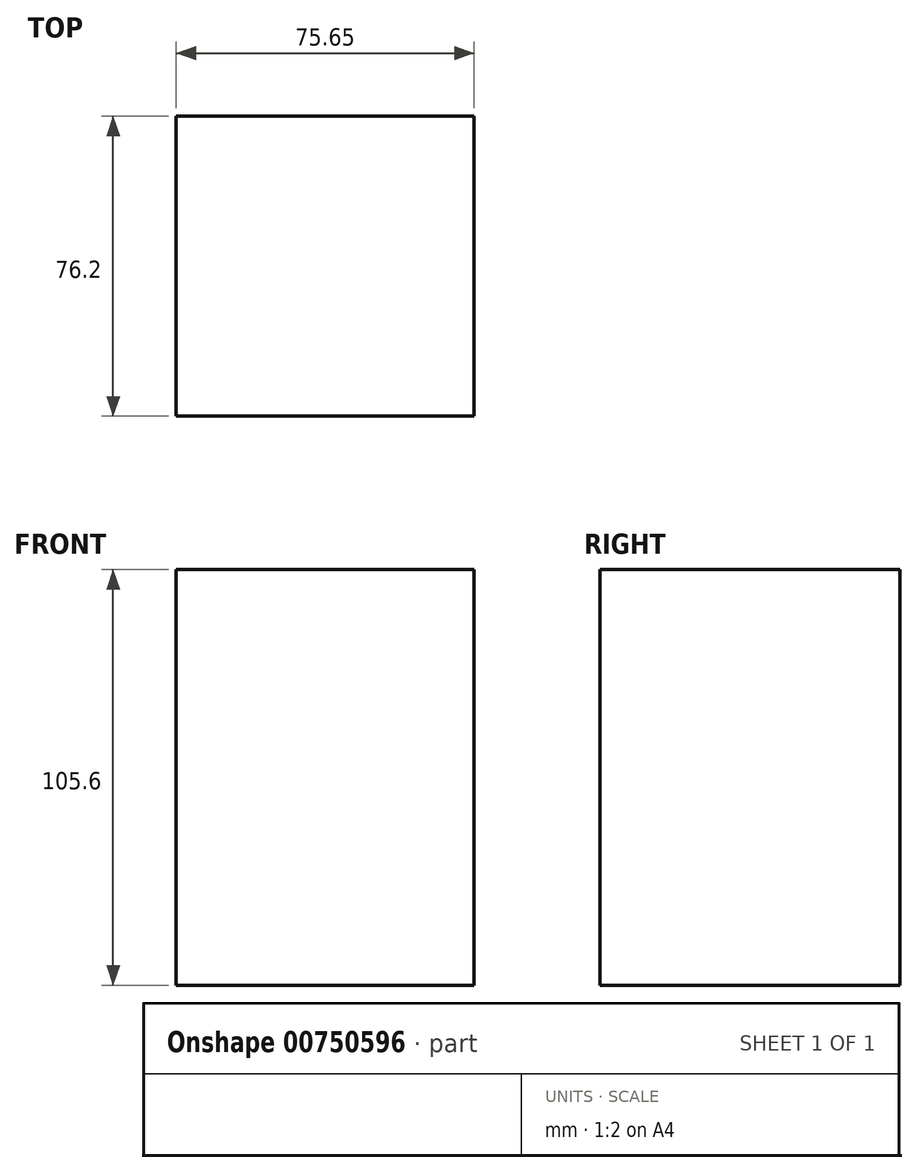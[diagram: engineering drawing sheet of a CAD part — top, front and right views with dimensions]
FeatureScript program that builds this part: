
annotation { "Feature Type Name" : "Feature", "Feature Type Description" : "" }
export const myFeature = defineFeature(function(context is Context, id is Id, definition is map)
    precondition{}
    {
        {
            var Q0;
            Q0=qCreatedBy(makeId("Front.planeOp"),FACE);
            var sketch = newSketch(context, id + "F0", { "sketchPlane" : qUnion([Q0])});
            skLineSegment(sketch, "E0.bottom", {"start": v(-38.96, 42.94) * mm, "end": v(36.69, 42.94) * mm});
            skLineSegment(sketch, "E0.top", {"start": v(-38.96, -62.66) * mm, "end": v(36.69, -62.66) * mm});
            skLineSegment(sketch, "E0.left", {"start": v(-38.96, 42.94) * mm, "end": v(-38.96, -62.66) * mm});
            skLineSegment(sketch, "E0.right", {"start": v(36.69, 42.94) * mm, "end": v(36.69, -62.66) * mm});
            skSolve(sketch);
        }
        {
            var Q0;
            Q0=makeQuery(id+"F0.imprint","IMPRINT",FACE,{"disambiguationData":[TD([[makeQuery(id+"F0.imprint","IMPRINT",EDGE,{"derivedFrom":sQuery(id+"F0.wireOp",EDGE,"E0.bottom")}),-1.0]])]});
            extrude(context, id + "F1", {"entities" : qUnion([Q0]), "depth" : 76.2 * mm, "offsetDistance" : 25.4 * mm});
        }
    });
